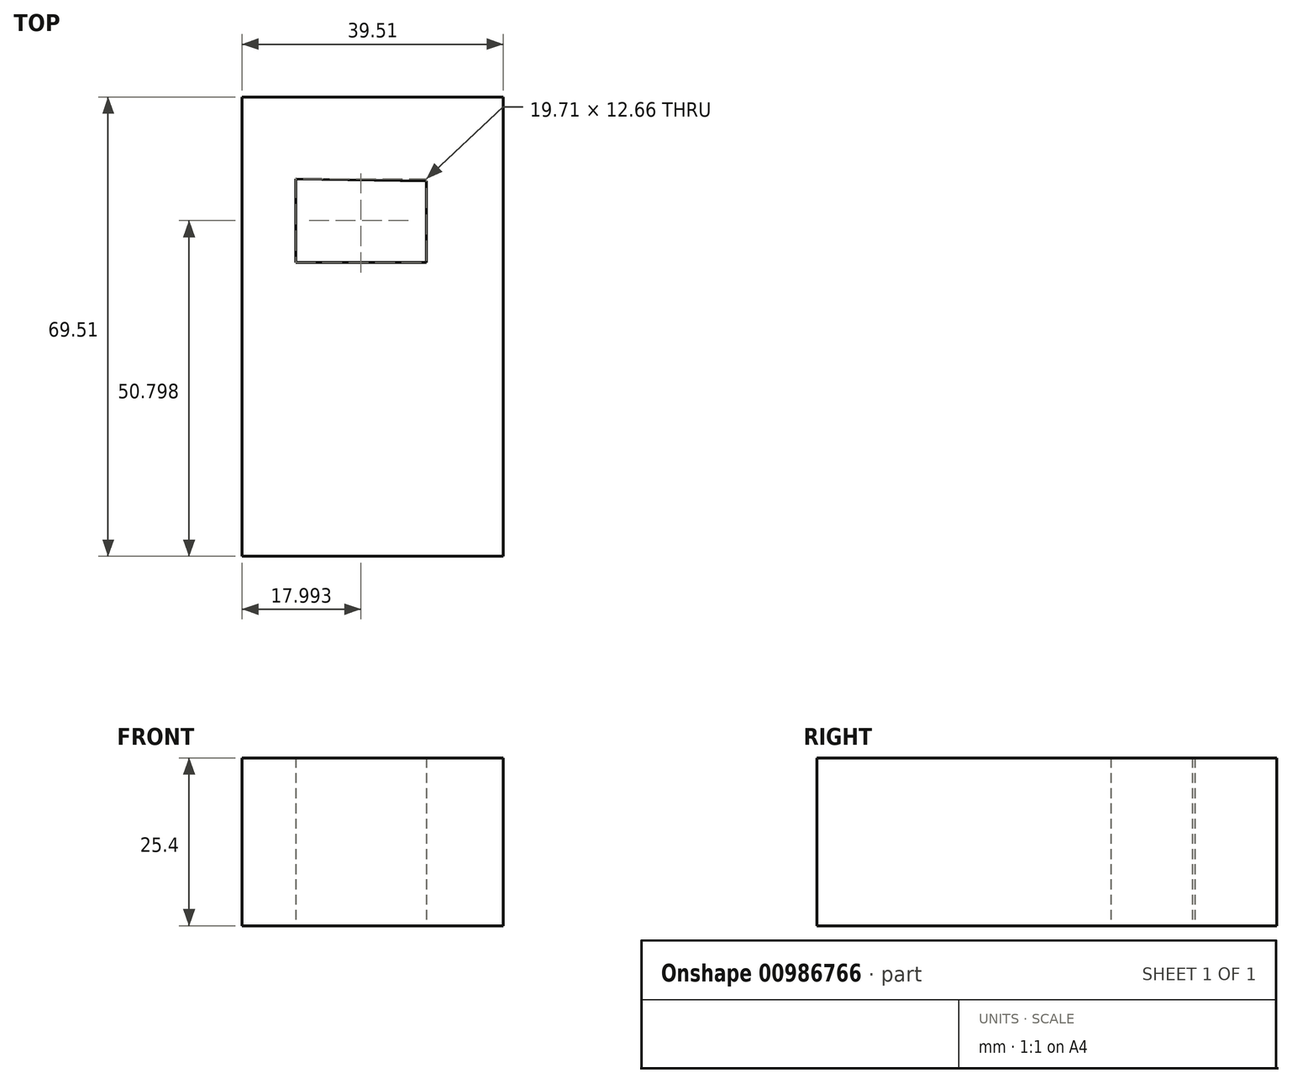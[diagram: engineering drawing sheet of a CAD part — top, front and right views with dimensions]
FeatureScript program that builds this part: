
annotation { "Feature Type Name" : "Feature", "Feature Type Description" : "" }
export const myFeature = defineFeature(function(context is Context, id is Id, definition is map)
    precondition{}
    {
        {
            var Q0;
            Q0=qCreatedBy(makeId("Top.planeOp"),FACE);
            var sketch = newSketch(context, id + "F0", { "sketchPlane" : qUnion([Q0])});
            skLineSegment(sketch, "E0", {"start": v(11.66, 56.55) * mm, "end": v(0, 44.47) * mm});
            skLineSegment(sketch, "E1", {"start": v(0, 44.47) * mm, "end": v(-19.71, 57.13) * mm});
            skLineSegment(sketch, "E2", {"start": v(-19.71, 57.13) * mm, "end": v(-27.85, 44.47) * mm});
            skLineSegment(sketch, "E3", {"start": v(11.66, 56.55) * mm, "end": v(-19.71, 57.13) * mm});
            skLineSegment(sketch, "E4", {"start": v(-27.85, 44.47) * mm, "end": v(0, 44.47) * mm});
            skLineSegment(sketch, "E5", {"start": v(0, 44.47) * mm, "end": v(0, 0) * mm});
            skLineSegment(sketch, "E6", {"start": v(11.66, 56.55) * mm, "end": v(11.66, 0) * mm});
            skLineSegment(sketch, "E7", {"start": v(-27.85, 44.47) * mm, "end": v(-27.85, 0) * mm});
            skLineSegment(sketch, "E8", {"start": v(-19.71, 57.13) * mm, "end": v(-19.71, 0) * mm});
            skLineSegment(sketch, "E9", {"start": v(-27.85, 0) * mm, "end": v(11.66, 0) * mm});
            skLineSegment(sketch, "E10", {"start": v(-19.71, 57.13) * mm, "end": v(-19.71, 68.93) * mm});
            skLineSegment(sketch, "E11", {"start": v(-27.85, 44.47) * mm, "end": v(-27.85, 69.5) * mm});
            skLineSegment(sketch, "E12", {"start": v(0, 44.47) * mm, "end": v(0, 69.5) * mm});
            skLineSegment(sketch, "E13", {"start": v(11.66, 56.55) * mm, "end": v(11.66, 69.5) * mm});
            skLineSegment(sketch, "E14", {"start": v(-27.85, 69.5) * mm, "end": v(11.66, 69.5) * mm});
            skSolve(sketch);
        }
        {
            var Q0;
            Q0 = qSketchRegion(id + "F0", true);
            extrude(context, id + "F1", {"entities" : qUnion([Q0]), "depth" : 25.4 * mm, "offsetDistance" : 25.4 * mm});
        }
    });
